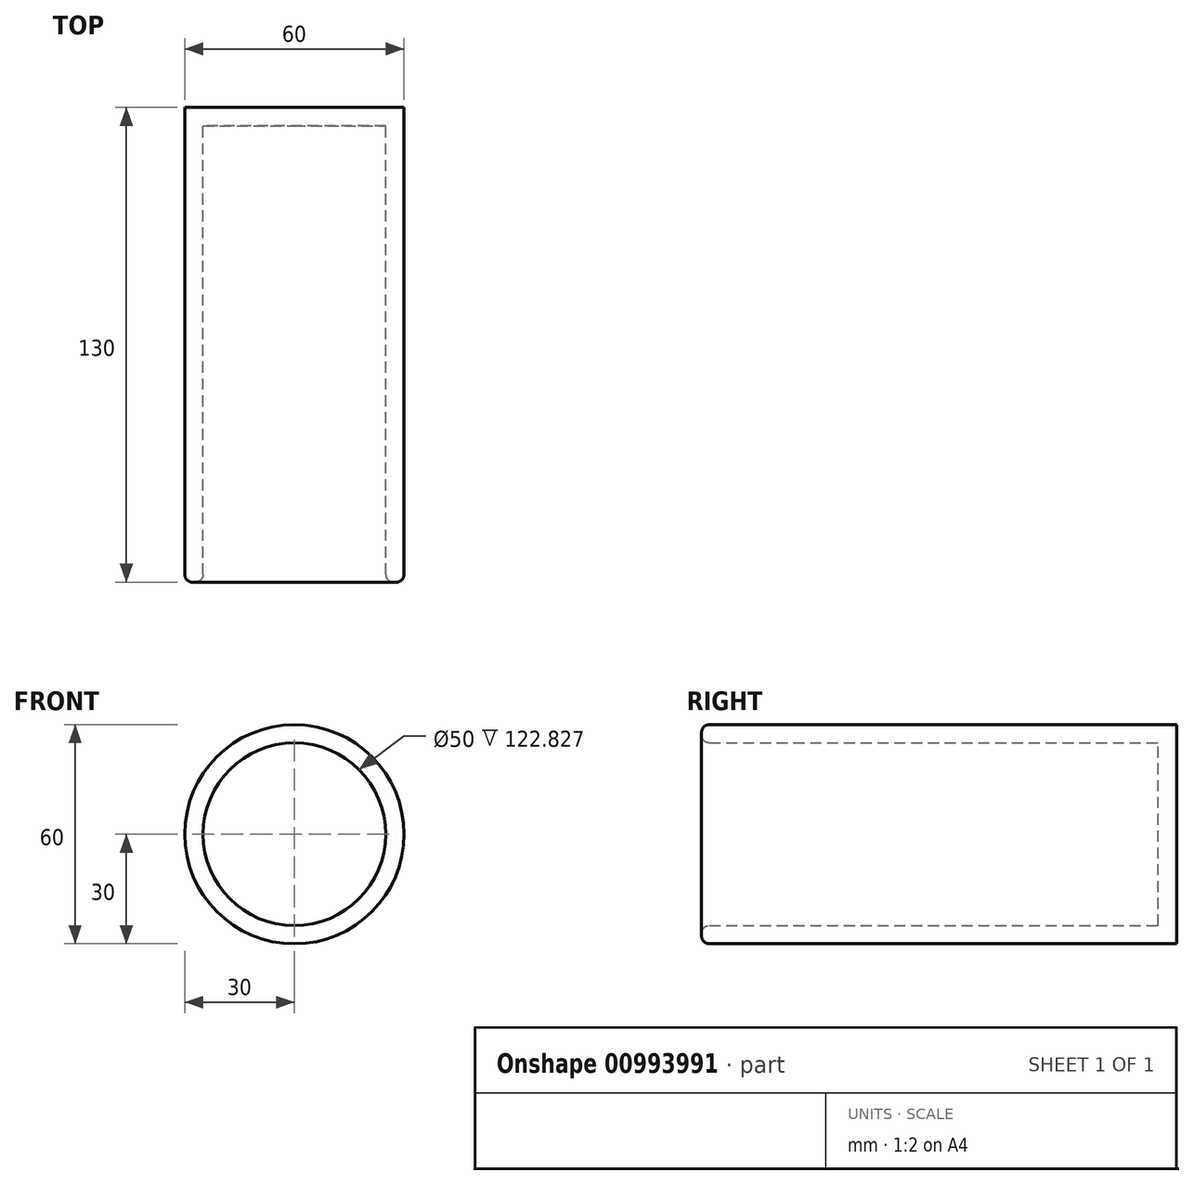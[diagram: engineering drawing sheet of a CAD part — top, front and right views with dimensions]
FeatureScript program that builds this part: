
annotation { "Feature Type Name" : "Feature", "Feature Type Description" : "" }
export const myFeature = defineFeature(function(context is Context, id is Id, definition is map)
    precondition{}
    {
        {
            var Q0;
            Q0=qCreatedBy(makeId("Front.planeOp"),FACE);
            var sketch = newSketch(context, id + "F0", { "sketchPlane" : qUnion([Q0])});
            skCircle(sketch, "E0", {"center": v(0, 0) * mm, "radius": 25 * mm});
            skCircle(sketch, "E1", {"center": v(0, 0) * mm, "radius": 30 * mm});
            skSolve(sketch);
        }
        {
            var Q0;
            Q0 = qSketchRegion(id + "F0", true);
            var Q1;
            Q1=makeQuery(id+"F0.imprint","IMPRINT",FACE,{"disambiguationData":[TD([[makeQuery(id+"F0.imprint","IMPRINT",EDGE,{"derivedFrom":sQuery(id+"F0.wireOp",EDGE,"E0")}),1.0]])]});
            extrude(context, id + "F1", {"entities" : qUnion([Q0, Q1]), "depth" : 5 * mm, "offsetDistance" : 25 * mm});
        }
        {
            var Q0;
            Q0 = qSketchRegion(id + "F0", true);
            extrude(context, id + "F2", {"entities" : qUnion([Q0]), "operationType" : NewBodyOperationType.ADD, "depth" : 130 * mm, "offsetDistance" : 25 * mm});
        }
        {
            var Q0;
            Q0=makeQuery(id+"F2.opExtrude","CAP_EDGE",EDGE,{"disambiguationData":[OSD([sQuery(id+"F0.wireOp",EDGE,"E1")])],"isStart":false});
            fillet(context, id + "F3", {"entities" : qUnion([Q0]), "radius" : 2.17 * mm, "tangentPropagation" : true, "allowEdgeOverflow" : false});
        }
        {
            var Q0;
            Q0=makeQuery(id+"F2.opExtrude","CAP_EDGE",EDGE,{"disambiguationData":[OSD([sQuery(id+"F0.wireOp",EDGE,"E0")])],"isStart":false});
            fillet(context, id + "F4", {"entities" : qUnion([Q0]), "radius" : 2.17 * mm, "tangentPropagation" : true, "allowEdgeOverflow" : false});
        }
    });
